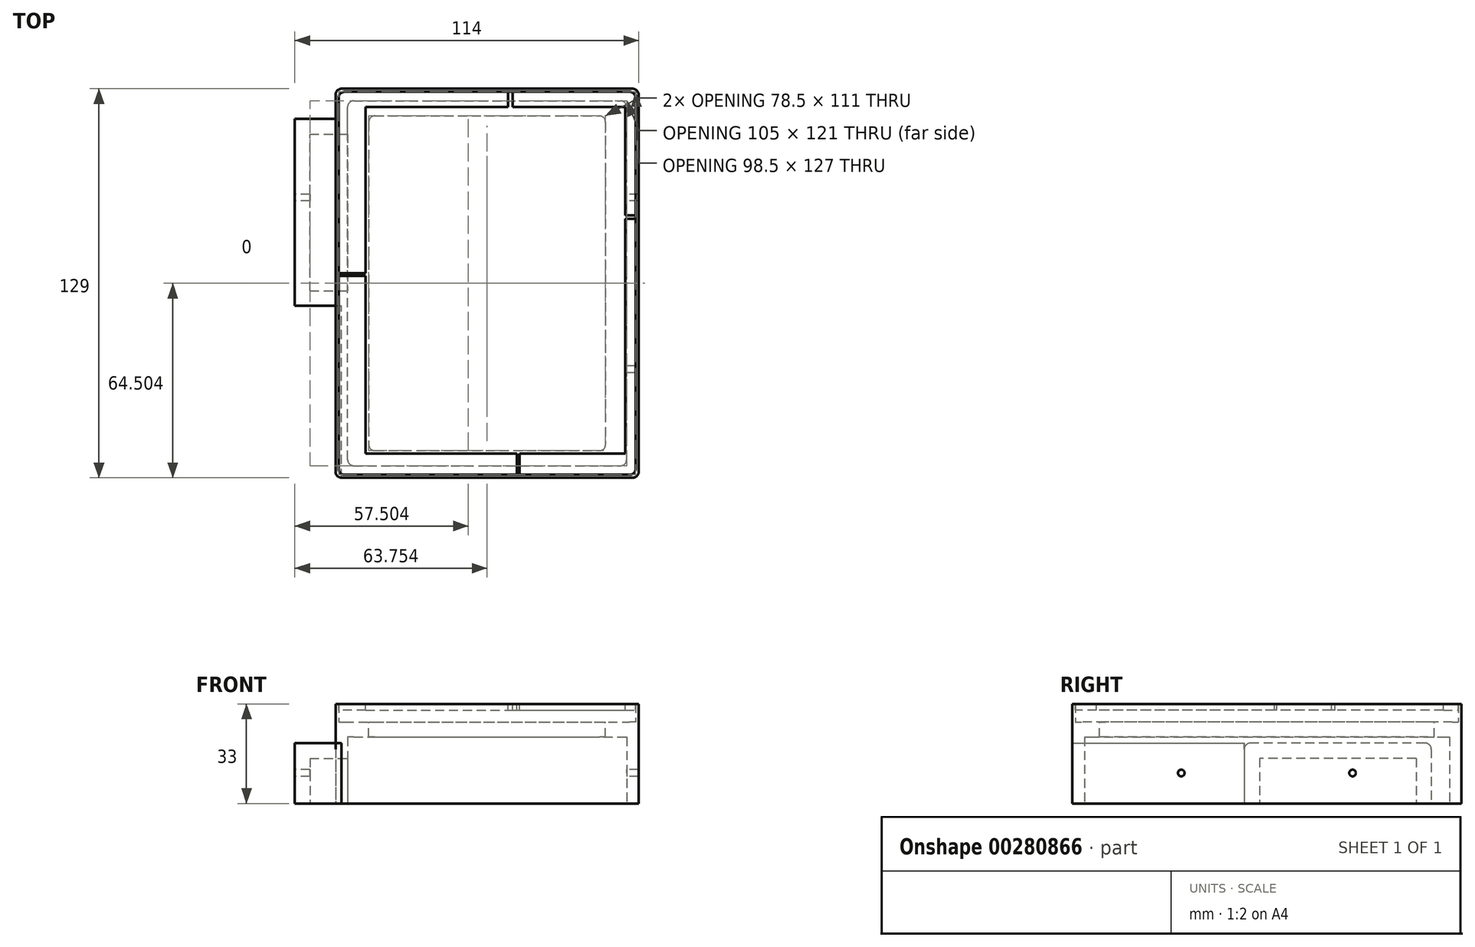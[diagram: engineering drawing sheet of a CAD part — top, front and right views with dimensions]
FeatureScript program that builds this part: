
annotation { "Feature Type Name" : "Feature", "Feature Type Description" : "" }
export const myFeature = defineFeature(function(context is Context, id is Id, definition is map)
    precondition{}
    {
        {
            var Q0;
            Q0=qCreatedBy(makeId("Top.planeOp"),FACE);
            var sketch = newSketch(context, id + "F0", { "sketchPlane" : qUnion([Q0])});
            skLineSegment(sketch, "E0.bottom", {"start": v(-48.46, 64.26) * mm, "end": v(46.04, 64.26) * mm});
            skLineSegment(sketch, "E0.top", {"start": v(-48.46, -62.74) * mm, "end": v(46.04, -62.74) * mm});
            skLineSegment(sketch, "E0.left", {"start": v(-50.46, 62.26) * mm, "end": v(-50.46, -60.74) * mm});
            skLineSegment(sketch, "E0.right", {"start": v(48.04, 62.26) * mm, "end": v(48.04, -60.74) * mm});
            skLineSegment(sketch, "E1.bottom", {"start": v(-49.46, 65.26) * mm, "end": v(47.04, 65.26) * mm});
            skLineSegment(sketch, "E1.top", {"start": v(-49.46, -63.74) * mm, "end": v(47.04, -63.74) * mm});
            skLineSegment(sketch, "E1.left", {"start": v(-51.46, 63.26) * mm, "end": v(-51.46, -61.74) * mm});
            skLineSegment(sketch, "E1.right", {"start": v(49.04, 63.26) * mm, "end": v(49.04, -61.74) * mm});
            skPoint(sketch, "E2.visualSharp", {"position": v(48.04, 64.26) * mm});
            skArc(sketch, "E2.filletArc", {"start": v(48.04, 62.26) * mm, "mid": v(47.46, 63.68) * mm, "end": v(46.04, 64.26) * mm});
            skPoint(sketch, "E3.visualSharp", {"position": v(49.04, 65.26) * mm});
            skArc(sketch, "E3.filletArc", {"start": v(49.04, 63.26) * mm, "mid": v(48.46, 64.68) * mm, "end": v(47.04, 65.26) * mm});
            skPoint(sketch, "E4.visualSharp", {"position": v(-50.46, 64.26) * mm});
            skArc(sketch, "E4.filletArc", {"start": v(-48.46, 64.26) * mm, "mid": v(-49.87, 63.68) * mm, "end": v(-50.46, 62.26) * mm});
            skPoint(sketch, "E5.visualSharp", {"position": v(-51.46, 65.26) * mm});
            skArc(sketch, "E5.filletArc", {"start": v(-49.46, 65.26) * mm, "mid": v(-50.87, 64.68) * mm, "end": v(-51.46, 63.26) * mm});
            skPoint(sketch, "E6.visualSharp", {"position": v(48.04, -62.74) * mm});
            skArc(sketch, "E6.filletArc", {"start": v(46.04, -62.74) * mm, "mid": v(47.46, -62.15) * mm, "end": v(48.04, -60.74) * mm});
            skPoint(sketch, "E7.visualSharp", {"position": v(49.04, -63.74) * mm});
            skArc(sketch, "E7.filletArc", {"start": v(47.04, -63.74) * mm, "mid": v(48.46, -63.15) * mm, "end": v(49.04, -61.74) * mm});
            skPoint(sketch, "E8.visualSharp", {"position": v(-50.46, -62.74) * mm});
            skArc(sketch, "E8.filletArc", {"start": v(-50.46, -60.74) * mm, "mid": v(-49.87, -62.15) * mm, "end": v(-48.46, -62.74) * mm});
            skPoint(sketch, "E9.visualSharp", {"position": v(-51.46, -63.74) * mm});
            skArc(sketch, "E9.filletArc", {"start": v(-51.46, -61.74) * mm, "mid": v(-50.87, -63.15) * mm, "end": v(-49.46, -63.74) * mm});
            skSolve(sketch);
        }
        {
            var Q0;
            Q0=qSketchRegion(id+"F0",true);
            extrude(context, id + "F1", {"entities" : qUnion([Q0]), "depth" : 6 * mm});
        }
        {
            var Q0;
            Q0=qCreatedBy(makeId("Top.planeOp"),FACE);
            var sketch = newSketch(context, id + "F2", { "sketchPlane" : qUnion([Q0])});
            skLineSegment(sketch, "E10.bottom", {"start": v(-49.46, 65.26) * mm, "end": v(47.04, 65.26) * mm});
            skLineSegment(sketch, "E10.top", {"start": v(-49.46, -63.74) * mm, "end": v(47.04, -63.74) * mm});
            skLineSegment(sketch, "E10.left", {"start": v(-51.46, 63.26) * mm, "end": v(-51.46, -61.74) * mm});
            skLineSegment(sketch, "E10.right", {"start": v(49.04, 63.26) * mm, "end": v(49.04, -61.74) * mm});
            skLineSegment(sketch, "E11.bottom", {"start": v(-38.46, 56.26) * mm, "end": v(36.04, 56.26) * mm});
            skLineSegment(sketch, "E11.top", {"start": v(-38.46, -54.74) * mm, "end": v(36.04, -54.74) * mm});
            skLineSegment(sketch, "E11.left", {"start": v(-40.46, 54.26) * mm, "end": v(-40.46, -52.74) * mm});
            skLineSegment(sketch, "E11.right", {"start": v(38.04, 54.26) * mm, "end": v(38.04, -52.74) * mm});
            skPoint(sketch, "E12.visualSharp", {"position": v(-40.46, -54.74) * mm});
            skArc(sketch, "E12.filletArc", {"start": v(-40.46, -52.74) * mm, "mid": v(-39.87, -54.15) * mm, "end": v(-38.46, -54.74) * mm});
            skPoint(sketch, "E13.visualSharp", {"position": v(38.04, -54.74) * mm});
            skArc(sketch, "E13.filletArc", {"start": v(36.04, -54.74) * mm, "mid": v(37.46, -54.15) * mm, "end": v(38.04, -52.74) * mm});
            skPoint(sketch, "E14.visualSharp", {"position": v(38.04, 56.26) * mm});
            skArc(sketch, "E14.filletArc", {"start": v(38.04, 54.26) * mm, "mid": v(37.46, 55.68) * mm, "end": v(36.04, 56.26) * mm});
            skPoint(sketch, "E15.visualSharp", {"position": v(-40.46, 56.26) * mm});
            skArc(sketch, "E15.filletArc", {"start": v(-38.46, 56.26) * mm, "mid": v(-39.87, 55.68) * mm, "end": v(-40.46, 54.26) * mm});
            skPoint(sketch, "E16.visualSharp", {"position": v(-51.46, -63.74) * mm});
            skArc(sketch, "E16.filletArc", {"start": v(-51.46, -61.74) * mm, "mid": v(-50.87, -63.15) * mm, "end": v(-49.46, -63.74) * mm});
            skPoint(sketch, "E17.visualSharp", {"position": v(49.04, -63.74) * mm});
            skArc(sketch, "E17.filletArc", {"start": v(47.04, -63.74) * mm, "mid": v(48.46, -63.15) * mm, "end": v(49.04, -61.74) * mm});
            skPoint(sketch, "E18.visualSharp", {"position": v(49.04, 65.26) * mm});
            skArc(sketch, "E18.filletArc", {"start": v(49.04, 63.26) * mm, "mid": v(48.46, 64.68) * mm, "end": v(47.04, 65.26) * mm});
            skPoint(sketch, "E19.visualSharp", {"position": v(-51.46, 65.26) * mm});
            skArc(sketch, "E19.filletArc", {"start": v(-49.46, 65.26) * mm, "mid": v(-50.87, 64.68) * mm, "end": v(-51.46, 63.26) * mm});
            skSolve(sketch);
        }
        {
            var Q0;
            Q0=qSketchRegion(id+"F2",true);
            extrude(context, id + "F3", {"entities" : qUnion([Q0]), "operationType" : NewBodyOperationType.ADD, "oppositeDirection" : true, "depth" : 2 * mm});
        }
        {
            var Q0;
            Q0=makeQuery(id+"F3.opExtrude","CAP_FACE",FACE,{"disambiguationData":[OSD([sQuery(id+"F2.wireOp",EDGE,"E10.bottom"),sQuery(id+"F2.wireOp",EDGE,"E10.top"),sQuery(id+"F2.wireOp",EDGE,"E10.left"),sQuery(id+"F2.wireOp",EDGE,"E10.right"),sQuery(id+"F2.wireOp",EDGE,"E11.bottom"),sQuery(id+"F2.wireOp",EDGE,"E11.top"),sQuery(id+"F2.wireOp",EDGE,"E11.left"),sQuery(id+"F2.wireOp",EDGE,"E11.right"),sQuery(id+"F2.wireOp",EDGE,"E12.filletArc"),sQuery(id+"F2.wireOp",EDGE,"E13.filletArc"),sQuery(id+"F2.wireOp",EDGE,"E14.filletArc"),sQuery(id+"F2.wireOp",EDGE,"E15.filletArc"),sQuery(id+"F2.wireOp",EDGE,"E16.filletArc"),sQuery(id+"F2.wireOp",EDGE,"E17.filletArc"),sQuery(id+"F2.wireOp",EDGE,"E18.filletArc"),sQuery(id+"F2.wireOp",EDGE,"E19.filletArc")])],"isStart":false});
            extrude(context, id + "F4", {"entities" : qUnion([Q0]), "operationType" : NewBodyOperationType.ADD, "depth" : 25 * mm});
        }
        {
            var Q0;
            Q0=makeQuery(id+"F4.opExtrude","CAP_FACE",FACE,{"disambiguationData":[OSD([sQuery(id+"F2.wireOp",EDGE,"E10.bottom"),sQuery(id+"F2.wireOp",EDGE,"E10.top"),sQuery(id+"F2.wireOp",EDGE,"E10.left"),sQuery(id+"F2.wireOp",EDGE,"E10.right"),sQuery(id+"F2.wireOp",EDGE,"E11.bottom"),sQuery(id+"F2.wireOp",EDGE,"E11.top"),sQuery(id+"F2.wireOp",EDGE,"E11.left"),sQuery(id+"F2.wireOp",EDGE,"E11.right"),sQuery(id+"F2.wireOp",EDGE,"E12.filletArc"),sQuery(id+"F2.wireOp",EDGE,"E13.filletArc"),sQuery(id+"F2.wireOp",EDGE,"E14.filletArc"),sQuery(id+"F2.wireOp",EDGE,"E15.filletArc"),sQuery(id+"F2.wireOp",EDGE,"E16.filletArc"),sQuery(id+"F2.wireOp",EDGE,"E17.filletArc"),sQuery(id+"F2.wireOp",EDGE,"E18.filletArc"),sQuery(id+"F2.wireOp",EDGE,"E19.filletArc")])],"isStart":false});
            var sketch = newSketch(context, id + "F5", { "sketchPlane" : qUnion([Q0])});
            skLineSegment(sketch, "E20.bottom", {"start": v(-45.46, 59.74) * mm, "end": v(43.04, 59.74) * mm});
            skLineSegment(sketch, "E20.top", {"start": v(-45.46, -61.26) * mm, "end": v(43.04, -61.26) * mm});
            skLineSegment(sketch, "E20.left", {"start": v(-47.46, 57.74) * mm, "end": v(-47.46, -59.26) * mm});
            skLineSegment(sketch, "E20.right", {"start": v(45.04, 57.74) * mm, "end": v(45.04, -59.26) * mm});
            skPoint(sketch, "E21.visualSharp", {"position": v(-47.46, 59.74) * mm});
            skArc(sketch, "E21.filletArc", {"start": v(-45.46, 59.74) * mm, "mid": v(-46.87, 59.15) * mm, "end": v(-47.46, 57.74) * mm});
            skPoint(sketch, "E22.visualSharp", {"position": v(45.04, 59.74) * mm});
            skArc(sketch, "E22.filletArc", {"start": v(45.04, 57.74) * mm, "mid": v(44.46, 59.15) * mm, "end": v(43.04, 59.74) * mm});
            skPoint(sketch, "E23.visualSharp", {"position": v(-47.46, -61.26) * mm});
            skArc(sketch, "E23.filletArc", {"start": v(-47.46, -59.26) * mm, "mid": v(-46.87, -60.68) * mm, "end": v(-45.46, -61.26) * mm});
            skPoint(sketch, "E24.visualSharp", {"position": v(45.04, -61.26) * mm});
            skArc(sketch, "E24.filletArc", {"start": v(43.04, -61.26) * mm, "mid": v(44.46, -60.68) * mm, "end": v(45.04, -59.26) * mm});
            skSolve(sketch);
        }
        {
            var Q0;
            Q0=qSketchRegion(id+"F5",true);
            extrude(context, id + "F6", {"entities" : qUnion([Q0]), "operationType" : NewBodyOperationType.REMOVE, "oppositeDirection" : true, "depth" : 22 * mm});
        }
        {
            var Q0;
            Q0=makeQuery(id+"F1.opExtrude","CAP_FACE",FACE,{"disambiguationData":[OSD([sQuery(id+"F0.wireOp",EDGE,"E0.bottom"),sQuery(id+"F0.wireOp",EDGE,"E0.top"),sQuery(id+"F0.wireOp",EDGE,"E0.left"),sQuery(id+"F0.wireOp",EDGE,"E0.right"),sQuery(id+"F0.wireOp",EDGE,"E1.bottom"),sQuery(id+"F0.wireOp",EDGE,"E1.top"),sQuery(id+"F0.wireOp",EDGE,"E1.left"),sQuery(id+"F0.wireOp",EDGE,"E1.right"),sQuery(id+"F0.wireOp",EDGE,"E2.filletArc"),sQuery(id+"F0.wireOp",EDGE,"E3.filletArc"),sQuery(id+"F0.wireOp",EDGE,"E4.filletArc"),sQuery(id+"F0.wireOp",EDGE,"E5.filletArc"),sQuery(id+"F0.wireOp",EDGE,"E6.filletArc"),sQuery(id+"F0.wireOp",EDGE,"E7.filletArc"),sQuery(id+"F0.wireOp",EDGE,"E8.filletArc"),sQuery(id+"F0.wireOp",EDGE,"E9.filletArc")])],"isStart":false});
            var sketch = newSketch(context, id + "F7", { "sketchPlane" : qUnion([Q0])});
            skLineSegment(sketch, "E25.bottom", {"start": v(-41.46, 59.26) * mm, "end": v(44.54, 59.26) * mm});
            skLineSegment(sketch, "E25.top", {"start": v(-41.46, -55.74) * mm, "end": v(44.54, -55.74) * mm});
            skLineSegment(sketch, "E25.left", {"start": v(-41.46, 59.26) * mm, "end": v(-41.46, -55.74) * mm});
            skLineSegment(sketch, "E25.right", {"start": v(44.54, 59.26) * mm, "end": v(44.54, -55.74) * mm});
            skLineSegment(sketch, "E26.bottom", {"start": v(5.73, 59.26) * mm, "end": v(7.27, 59.26) * mm});
            skLineSegment(sketch, "E26.top", {"start": v(5.73, 64.26) * mm, "end": v(7.27, 64.26) * mm});
            skLineSegment(sketch, "E26.left", {"start": v(7.27, 59.26) * mm, "end": v(7.27, 64.26) * mm});
            skLineSegment(sketch, "E26.right", {"start": v(5.73, 59.26) * mm, "end": v(5.73, 64.26) * mm});
            skLineSegment(sketch, "E27.bottom", {"start": v(-41.46, 4.07) * mm, "end": v(-50.46, 4.07) * mm});
            skLineSegment(sketch, "E27.top", {"start": v(-41.46, 3.27) * mm, "end": v(-50.46, 3.27) * mm});
            skLineSegment(sketch, "E27.left", {"start": v(-41.46, 4.07) * mm, "end": v(-41.46, 3.27) * mm});
            skLineSegment(sketch, "E27.right", {"start": v(-50.46, 4.07) * mm, "end": v(-50.46, 3.27) * mm});
            skLineSegment(sketch, "E28.bottom", {"start": v(8.66, -55.74) * mm, "end": v(9.49, -55.74) * mm});
            skLineSegment(sketch, "E28.top", {"start": v(8.66, -62.74) * mm, "end": v(9.49, -62.74) * mm});
            skLineSegment(sketch, "E28.left", {"start": v(8.66, -55.74) * mm, "end": v(8.66, -62.74) * mm});
            skLineSegment(sketch, "E28.right", {"start": v(9.49, -55.74) * mm, "end": v(9.49, -62.74) * mm});
            skLineSegment(sketch, "E29.bottom", {"start": v(44.54, 23.35) * mm, "end": v(48.04, 23.35) * mm});
            skLineSegment(sketch, "E29.top", {"start": v(44.54, 22.14) * mm, "end": v(48.04, 22.14) * mm});
            skLineSegment(sketch, "E29.left", {"start": v(44.54, 23.35) * mm, "end": v(44.54, 22.14) * mm});
            skLineSegment(sketch, "E29.right", {"start": v(48.04, 23.35) * mm, "end": v(48.04, 22.14) * mm});
            skSolve(sketch);
        }
        {
            var Q0;
            Q0=qSketchRegion(id+"F7",true);
            extrude(context, id + "F8", {"entities" : qUnion([Q0]), "oppositeDirection" : true, "depth" : 2 * mm});
        }
        {
            var Q0;
            {var subQ0=sQuery(id+"F2.wireOp",EDGE,"E10.left");Q0=makeQuery(id+"F4.boolean.opBoolean","MERGE",FACE,{"derivedFrom":[makeQuery(id+"F3.boolean.opBoolean","MERGE",FACE,{"derivedFrom":[makeQuery(id+"F1.opExtrude","SWEPT_FACE",FACE,{"disambiguationData":[OSD([sQuery(id+"F0.wireOp",EDGE,"E1.left")])]}),makeQuery(id+"F3.opExtrude","SWEPT_FACE",FACE,{"disambiguationData":[OSD([subQ0])]})]}),makeQuery(id+"F4.opExtrude","SWEPT_FACE",FACE,{"disambiguationData":[OSD([subQ0])]})]});}
            var sketch = newSketch(context, id + "F9", { "sketchPlane" : qUnion([Q0])});
            skLineSegment(sketch, "E30.bottom", {"start": v(-53.26, -7) * mm, "end": v(4.74, -7) * mm});
            skLineSegment(sketch, "E30.top", {"start": v(-55.26, -27) * mm, "end": v(6.74, -27) * mm});
            skLineSegment(sketch, "E30.left", {"start": v(-55.26, -9) * mm, "end": v(-55.26, -27) * mm});
            skLineSegment(sketch, "E30.right", {"start": v(6.74, -9) * mm, "end": v(6.74, -27) * mm});
            skPoint(sketch, "E31.visualSharp", {"position": v(-55.26, -7) * mm});
            skPoint(sketch, "E32.visualSharp", {"position": v(6.74, -7) * mm});
            skArc(sketch, "E33.filletArc", {"start": v(-53.26, -7) * mm, "mid": v(-54.68, -7.59) * mm, "end": v(-55.26, -9) * mm});
            skArc(sketch, "E34.filletArc", {"start": v(6.74, -9) * mm, "mid": v(6.15, -7.59) * mm, "end": v(4.74, -7) * mm});
            skSolve(sketch);
        }
        {
            var Q0;
            Q0=qSketchRegion(id+"F9",true);
            extrude(context, id + "F10", {"entities" : qUnion([Q0]), "operationType" : NewBodyOperationType.ADD, "depth" : 13.5 * mm});
        }
        {
            var Q0;
            Q0=makeQuery(id+"F10.boolean.opBoolean","MERGE",FACE,{"derivedFrom":[makeQuery(id+"F4.opExtrude","CAP_FACE",FACE,{"disambiguationData":[OSD([sQuery(id+"F2.wireOp",EDGE,"E10.bottom"),sQuery(id+"F2.wireOp",EDGE,"E10.top"),sQuery(id+"F2.wireOp",EDGE,"E10.left"),sQuery(id+"F2.wireOp",EDGE,"E10.right"),sQuery(id+"F2.wireOp",EDGE,"E11.bottom"),sQuery(id+"F2.wireOp",EDGE,"E11.top"),sQuery(id+"F2.wireOp",EDGE,"E11.left"),sQuery(id+"F2.wireOp",EDGE,"E11.right"),sQuery(id+"F2.wireOp",EDGE,"E12.filletArc"),sQuery(id+"F2.wireOp",EDGE,"E13.filletArc"),sQuery(id+"F2.wireOp",EDGE,"E14.filletArc"),sQuery(id+"F2.wireOp",EDGE,"E15.filletArc"),sQuery(id+"F2.wireOp",EDGE,"E16.filletArc"),sQuery(id+"F2.wireOp",EDGE,"E17.filletArc"),sQuery(id+"F2.wireOp",EDGE,"E18.filletArc"),sQuery(id+"F2.wireOp",EDGE,"E19.filletArc")])],"isStart":false}),makeQuery(id+"F10.opExtrude","SWEPT_FACE",FACE,{"disambiguationData":[OSD([sQuery(id+"F9.wireOp",EDGE,"E30.top")])]})]});
            var sketch = newSketch(context, id + "F11", { "sketchPlane" : qUnion([Q0])});
            skLineSegment(sketch, "E35.bottom", {"start": v(-79, 66.77) * mm, "end": v(-49.46, 66.77) * mm});
            skLineSegment(sketch, "E35.top", {"start": v(-79, 6.74) * mm, "end": v(-49.46, 6.74) * mm});
            skLineSegment(sketch, "E35.left", {"start": v(-79, 66.77) * mm, "end": v(-79, 6.74) * mm});
            skLineSegment(sketch, "E35.right", {"start": v(-49.46, 66.77) * mm, "end": v(-49.46, 6.74) * mm});
            skSolve(sketch);
        }
        {
            var Q0;
            Q0=qSketchRegion(id+"F11",true);
            extrude(context, id + "F12", {"entities" : qUnion([Q0]), "operationType" : NewBodyOperationType.REMOVE, "oppositeDirection" : true, "depth" : 20 * mm});
        }
        {
            var Q0;
            Q0=makeQuery(id+"F10.boolean.opBoolean","MERGE",FACE,{"derivedFrom":[makeQuery(id+"F4.opExtrude","CAP_FACE",FACE,{"disambiguationData":[OSD([sQuery(id+"F2.wireOp",EDGE,"E10.bottom"),sQuery(id+"F2.wireOp",EDGE,"E10.top"),sQuery(id+"F2.wireOp",EDGE,"E10.left"),sQuery(id+"F2.wireOp",EDGE,"E10.right"),sQuery(id+"F2.wireOp",EDGE,"E11.bottom"),sQuery(id+"F2.wireOp",EDGE,"E11.top"),sQuery(id+"F2.wireOp",EDGE,"E11.left"),sQuery(id+"F2.wireOp",EDGE,"E11.right"),sQuery(id+"F2.wireOp",EDGE,"E12.filletArc"),sQuery(id+"F2.wireOp",EDGE,"E13.filletArc"),sQuery(id+"F2.wireOp",EDGE,"E14.filletArc"),sQuery(id+"F2.wireOp",EDGE,"E15.filletArc"),sQuery(id+"F2.wireOp",EDGE,"E16.filletArc"),sQuery(id+"F2.wireOp",EDGE,"E17.filletArc"),sQuery(id+"F2.wireOp",EDGE,"E18.filletArc"),sQuery(id+"F2.wireOp",EDGE,"E19.filletArc")])],"isStart":false}),makeQuery(id+"F10.opExtrude","SWEPT_FACE",FACE,{"disambiguationData":[OSD([sQuery(id+"F9.wireOp",EDGE,"E30.top")])]})]});
            var sketch = newSketch(context, id + "F13", { "sketchPlane" : qUnion([Q0])});
            skLineSegment(sketch, "E36.bottom", {"start": v(-59.96, 1.74) * mm, "end": v(-35.72, 1.74) * mm});
            skLineSegment(sketch, "E36.top", {"start": v(-59.96, -50.26) * mm, "end": v(-35.72, -50.26) * mm});
            skLineSegment(sketch, "E36.left", {"start": v(-59.96, 1.74) * mm, "end": v(-59.96, -50.26) * mm});
            skLineSegment(sketch, "E36.right", {"start": v(-35.72, 1.74) * mm, "end": v(-35.72, -50.26) * mm});
            skSolve(sketch);
        }
        {
            var Q0;
            Q0=qSketchRegion(id+"F13",true);
            extrude(context, id + "F14", {"entities" : qUnion([Q0]), "operationType" : NewBodyOperationType.REMOVE, "oppositeDirection" : true, "depth" : 15 * mm});
        }
        {
            var Q0;
            Q0=makeQuery(id+"F10.opExtrude","CAP_FACE",FACE,{"disambiguationData":[OSD([sQuery(id+"F9.wireOp",EDGE,"E30.bottom"),sQuery(id+"F9.wireOp",EDGE,"E30.top"),sQuery(id+"F9.wireOp",EDGE,"E30.left"),sQuery(id+"F9.wireOp",EDGE,"E30.right"),sQuery(id+"F9.wireOp",EDGE,"E33.filletArc"),sQuery(id+"F9.wireOp",EDGE,"E34.filletArc")])],"isStart":false});
            var sketch = newSketch(context, id + "F15", { "sketchPlane" : qUnion([Q0])});
            skCircle(sketch, "E37", {"center": v(-29.16, -16.9) * mm, "radius": 1.1 * mm});
            skSolve(sketch);
        }
        {
            var Q0;
            {var subQ0=sQuery(id+"F2.wireOp",EDGE,"E10.right");Q0=makeQuery(id+"F4.boolean.opBoolean","MERGE",FACE,{"derivedFrom":[makeQuery(id+"F3.boolean.opBoolean","MERGE",FACE,{"derivedFrom":[makeQuery(id+"F1.opExtrude","SWEPT_FACE",FACE,{"disambiguationData":[OSD([sQuery(id+"F0.wireOp",EDGE,"E1.right")])]}),makeQuery(id+"F3.opExtrude","SWEPT_FACE",FACE,{"disambiguationData":[OSD([subQ0])]})]}),makeQuery(id+"F4.opExtrude","SWEPT_FACE",FACE,{"disambiguationData":[OSD([subQ0])]})]});}
            var sketch = newSketch(context, id + "F16", { "sketchPlane" : qUnion([Q0])});
            skCircle(sketch, "E38", {"center": v(-27.64, -16.9) * mm, "radius": 1.1 * mm});
            skSolve(sketch);
        }
        {
            var Q0;
            Q0=qSketchRegion(id+"F15",true);
            extrude(context, id + "F17", {"entities" : qUnion([Q0]), "operationType" : NewBodyOperationType.REMOVE, "oppositeDirection" : true, "depth" : 120 * mm});
        }
        {
            var Q0;
            Q0=qSketchRegion(id+"F16",true);
            extrude(context, id + "F18", {"entities" : qUnion([Q0]), "operationType" : NewBodyOperationType.REMOVE, "oppositeDirection" : true, "depth" : 25 * mm});
        }
        {
            var Q0;
            Q0=makeQuery(id+"F1.opExtrude","SWEPT_BODY",BODY,{"disambiguationData":[OSD([sQuery(id+"F0.wireOp",EDGE,"E0.bottom"),sQuery(id+"F0.wireOp",EDGE,"E0.top"),sQuery(id+"F0.wireOp",EDGE,"E0.left"),sQuery(id+"F0.wireOp",EDGE,"E0.right"),sQuery(id+"F0.wireOp",EDGE,"E1.bottom"),sQuery(id+"F0.wireOp",EDGE,"E1.top"),sQuery(id+"F0.wireOp",EDGE,"E1.left"),sQuery(id+"F0.wireOp",EDGE,"E1.right"),sQuery(id+"F0.wireOp",EDGE,"E2.filletArc"),sQuery(id+"F0.wireOp",EDGE,"E3.filletArc"),sQuery(id+"F0.wireOp",EDGE,"E4.filletArc"),sQuery(id+"F0.wireOp",EDGE,"E5.filletArc"),sQuery(id+"F0.wireOp",EDGE,"E6.filletArc"),sQuery(id+"F0.wireOp",EDGE,"E7.filletArc"),sQuery(id+"F0.wireOp",EDGE,"E8.filletArc"),sQuery(id+"F0.wireOp",EDGE,"E9.filletArc")])]});
            transform(context, id + "F19", {"entities" : qUnion([Q0]), "transformType" : TransformType.TRANSLATION_3D, "dx" : 0 * mm, "dy" : 0 * mm, "dz" : 0 * mm, "makeCopy" : true});
        }
    });
